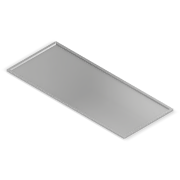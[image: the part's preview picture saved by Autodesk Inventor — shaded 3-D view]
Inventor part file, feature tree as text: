
AUTODESK INVENTOR PART (.ipt)
format: ipt  version: 2020.3 (Build 243373000, 373)  size: 346,112 bytes
history: native  units: mm
features: other x12, sheet_metal_op x4, sketch x4
ambient origin geometry x8: Origin, YZ Plane, XZ Plane, XY Plane, X Axis, Y Axis, Z Axis, Center Point
bodies: Body1 (feature_tree)
feature tree (20):
  other  "Sólido1"
  sheet_metal_op  "Face1"
  sheet_metal_op  "Flange1"
  sheet_metal_op  "Flange2"
  sheet_metal_op  "Flange3"
  sketch  "Esboço1"  dims[d0=2470.0mm]
  other  "Placa1"
  sketch  "Esboço2"  dims[d1=970.0mm]
  other  "Placa2"
  other  "Vergadura1"
  other  "Canto1"
  sketch  "Esboço3"  dims[d2=1.5mm]
  other  "Placa3"
  other  "Vergadura2"
  other  "Canto2"
  sketch  "Esboço4"  dims[d3=1.5mm d4=0.75mm d5=3.0mm d6=1.5mm d7=25.0mm d8=45.0deg d9=1.5mm d10=6.0mm d11=1.5mm d12=1.5mm d13=1.5mm d14=0.75mm d15=3.0mm d16=1.5mm d17=40.0mm d18=45.0deg d19=1.5mm d20=6.0mm d21=1.5mm d22=1.5mm d23=1.5mm d24=0.75mm d25=3.0mm d26=1.5mm d27=30.0mm d28=90.0deg d29=1.5mm d30=6.0mm d31=1.5mm d32=1.5mm]
  other  "Placa4"
  other  "Vergadura3"
  other  "Canto3"
  other  "Definição1"
